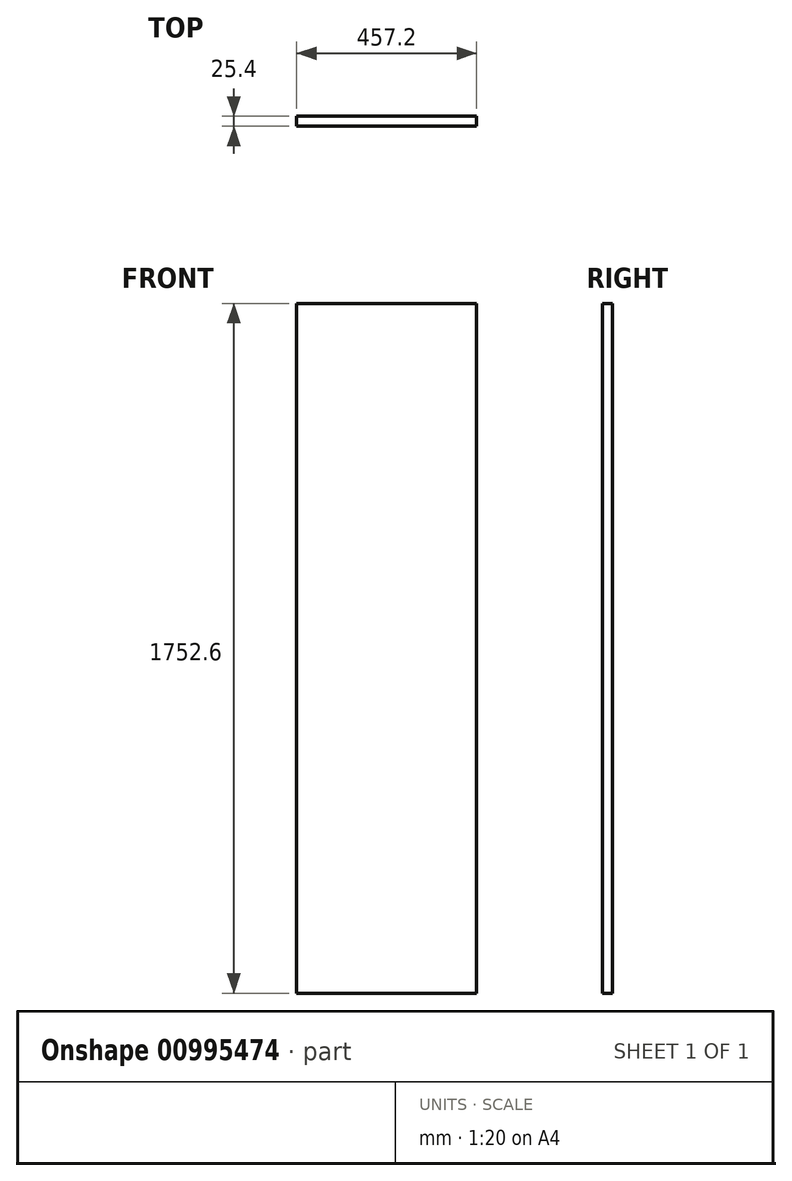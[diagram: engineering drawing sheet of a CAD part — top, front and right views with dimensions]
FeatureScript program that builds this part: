
annotation { "Feature Type Name" : "Feature", "Feature Type Description" : "" }
export const myFeature = defineFeature(function(context is Context, id is Id, definition is map)
    precondition{}
    {
        {
            var Q0;
            Q0=qCreatedBy(makeId("Front.planeOp"),FACE);
            var sketch = newSketch(context, id + "F0", { "sketchPlane" : qUnion([Q0])});
            skLineSegment(sketch, "E0.bottom", {"start": v(228.6, -876.3) * mm, "end": v(-228.6, -876.3) * mm});
            skLineSegment(sketch, "E0.top", {"start": v(228.6, 876.3) * mm, "end": v(-228.6, 876.3) * mm});
            skLineSegment(sketch, "E0.left", {"start": v(228.6, -876.3) * mm, "end": v(228.6, 876.3) * mm});
            skLineSegment(sketch, "E0.right", {"start": v(-228.6, -876.3) * mm, "end": v(-228.6, 876.3) * mm});
            skPoint(sketch, "E0.middle", {"position": v(0, 0) * mm});
            skSolve(sketch);
        }
        {
            var Q0;
            Q0 = qSketchRegion(id + "F0", true);
            extrude(context, id + "F1", {"entities" : qUnion([Q0]), "depth" : 25.4 * mm, "offsetDistance" : 25.4 * mm});
        }
    });
